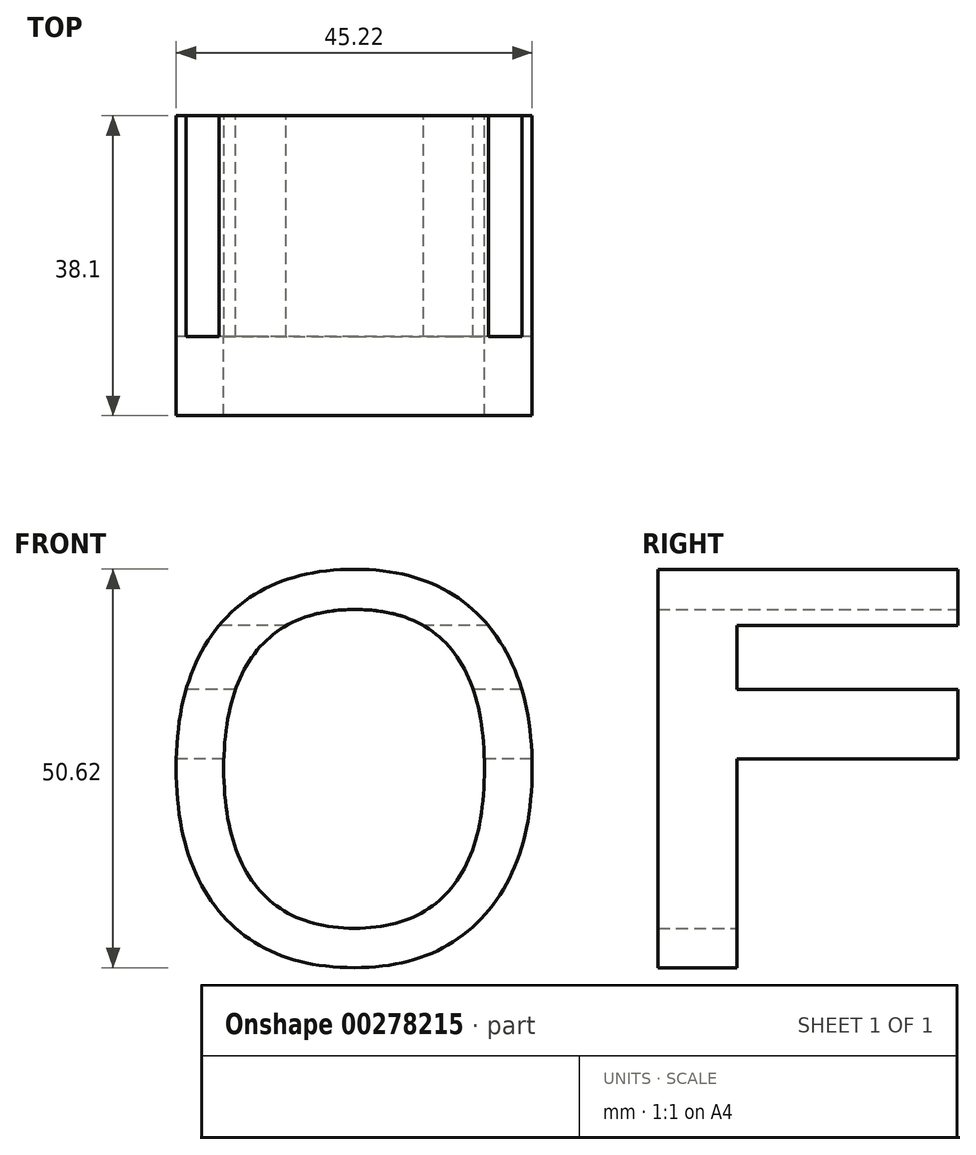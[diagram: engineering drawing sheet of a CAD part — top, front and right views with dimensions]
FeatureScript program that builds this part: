
annotation { "Feature Type Name" : "Feature", "Feature Type Description" : "" }
export const myFeature = defineFeature(function(context is Context, id is Id, definition is map)
    precondition{}
    {
        {
            var Q0;
            Q0=qCreatedBy(makeId("Front.planeOp"),FACE);
            var sketch = newSketch(context, id + "F0", { "sketchPlane" : qUnion([Q0])});
            skText(sketch, "E0", { "text": "O", "fontName": "OpenSans-Regular.ttf"});
            const initialGuessF0  = {"E0": [0.00055, -0.00074, 1, 0, 0.04958]};
            skSetInitialGuess(sketch, initialGuessF0);
            skSolve(sketch);
        }
        {
            var Q0;
            Q0 = qSketchRegion(id + "F0", true);
            extrude(context, id + "F1", {"entities" : qUnion([Q0]), "depth" : 38.1 * mm});
        }
        {
            var Q0;
            Q0=qCreatedBy(makeId("Right.planeOp"),FACE);
            var sketch = newSketch(context, id + "F2", { "sketchPlane" : qUnion([Q0])});
            skLineSegment(sketch, "E1.bottom", {"start": v(-28.06, 42.04) * mm, "end": v(0, 42.04) * mm});
            skLineSegment(sketch, "E1.top", {"start": v(-28.06, 33.91) * mm, "end": v(0, 33.91) * mm});
            skLineSegment(sketch, "E1.left", {"start": v(-28.06, 42.04) * mm, "end": v(-28.06, 33.91) * mm});
            skLineSegment(sketch, "E1.right", {"start": v(0, 42.04) * mm, "end": v(0, 33.91) * mm});
            skLineSegment(sketch, "E2.bottom", {"start": v(-28.06, 25.08) * mm, "end": v(0, 25.08) * mm});
            skLineSegment(sketch, "E2.top", {"start": v(-28.06, -4.54) * mm, "end": v(0, -4.54) * mm});
            skLineSegment(sketch, "E2.left", {"start": v(-28.06, 25.08) * mm, "end": v(-28.06, -4.54) * mm});
            skLineSegment(sketch, "E2.right", {"start": v(0, 25.08) * mm, "end": v(0, -4.54) * mm});
            skSolve(sketch);
        }
        {
            var Q0;
            Q0=makeQuery(id+"F2.imprint","IMPRINT",FACE,{"disambiguationData":[TD([[makeQuery(id+"F2.imprint","IMPRINT",EDGE,{"derivedFrom":sQuery(id+"F2.wireOp",EDGE,"E1.bottom")}),-1.0]])]});
            extrude(context, id + "F3", {"entities" : qUnion([Q0]), "operationType" : NewBodyOperationType.REMOVE, "depth" : 50.8 * mm});
        }
        {
            var Q0;
            Q0=makeQuery(id+"F2.imprint","IMPRINT",FACE,{"disambiguationData":[TD([[makeQuery(id+"F2.imprint","IMPRINT",EDGE,{"derivedFrom":sQuery(id+"F2.wireOp",EDGE,"E2.bottom")}),-1.0]])]});
            extrude(context, id + "F4", {"entities" : qUnion([Q0]), "operationType" : NewBodyOperationType.REMOVE, "depth" : 76.2 * mm});
        }
    });
